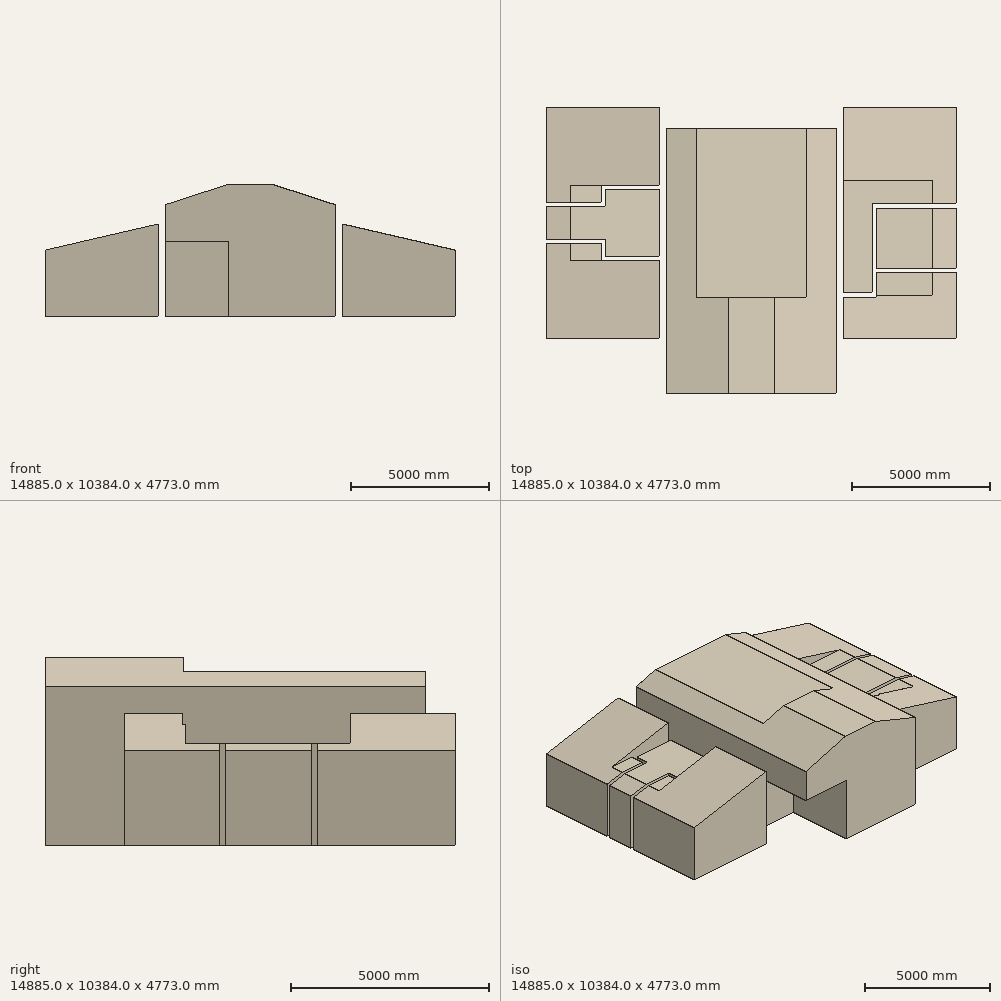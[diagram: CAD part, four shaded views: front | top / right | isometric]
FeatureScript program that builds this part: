
annotation { "Feature Type Name" : "Feature", "Feature Type Description" : "" }
export const myFeature = defineFeature(function(context is Context, id is Id, definition is map)
    precondition{}
    {
        {
            var Q0;
            Q0=qCreatedBy(makeId("Top.planeOp"),FACE);
            var sketch = newSketch(context, id + "F0", { "sketchPlane" : qUnion([Q0])});
            skLineSegment(sketch, "E0.bottom", {"start": v(1904.35, 18.05) * mm, "end": v(-95.65, 18.05) * mm});
            skLineSegment(sketch, "E0.top", {"start": v(3994.35, 3460.05) * mm, "end": v(-95.65, 3460.05) * mm});
            skLineSegment(sketch, "E0.left", {"start": v(3994.35, 618.05) * mm, "end": v(3994.35, 3460.05) * mm});
            skLineSegment(sketch, "E0.right", {"start": v(-95.65, 18.05) * mm, "end": v(-95.65, 3460.05) * mm});
            skLineSegment(sketch, "E1.top", {"start": v(3994.35, 618.05) * mm, "end": v(1904.35, 618.05) * mm});
            skLineSegment(sketch, "E1.right", {"start": v(1904.35, 18.05) * mm, "end": v(1904.35, 618.05) * mm});
            skSolve(sketch);
        }
        {
            var Q0;
            Q0 = qSketchRegion(id + "F0", true);
            extrude(context, id + "F1", {"entities" : qUnion([Q0]), "depth" : 4000 * mm, "offsetDistance" : 25 * mm});
        }
        {
            var Q0;
            Q0=makeQuery(id+"F1.opExtrude","CAP_FACE",FACE,{"disambiguationData":[OSD([sQuery(id+"F0.wireOp",EDGE,"E0.bottom"),sQuery(id+"F0.wireOp",EDGE,"E0.top"),sQuery(id+"F0.wireOp",EDGE,"E0.left"),sQuery(id+"F0.wireOp",EDGE,"E0.right"),sQuery(id+"F0.wireOp",EDGE,"E1.top"),sQuery(id+"F0.wireOp",EDGE,"E1.right")])],"isStart":true});
            var sketch = newSketch(context, id + "F2", { "sketchPlane" : qUnion([Q0])});
            skLineSegment(sketch, "E2", {"start": v(-95.65, 131.95) * mm, "end": v(2054.35, 131.95) * mm});
            skLineSegment(sketch, "E3", {"start": v(2054.35, 131.95) * mm, "end": v(2054.35, -468.05) * mm});
            skLineSegment(sketch, "E4", {"start": v(2054.35, -468.05) * mm, "end": v(3994.35, -468.05) * mm});
            skLineSegment(sketch, "E5", {"start": v(3994.35, -468.05) * mm, "end": v(3994.35, 1931.95) * mm});
            skLineSegment(sketch, "E6", {"start": v(3994.35, 1931.95) * mm, "end": v(2054.35, 1931.95) * mm});
            skLineSegment(sketch, "E7", {"start": v(2054.35, 1931.95) * mm, "end": v(2054.35, 1331.95) * mm});
            skLineSegment(sketch, "E8", {"start": v(2054.35, 1331.95) * mm, "end": v(-95.65, 1331.95) * mm});
            skLineSegment(sketch, "E9", {"start": v(-95.65, 1331.95) * mm, "end": v(-95.65, 131.95) * mm});
            skSolve(sketch);
        }
        {
            var Q0;
            Q0 = qSketchRegion(id + "F2", true);
            extrude(context, id + "F3", {"entities" : qUnion([Q0]), "oppositeDirection" : true, "depth" : 4000 * mm, "offsetDistance" : 25 * mm});
        }
        {
            var Q0;
            Q0=makeQuery(id+"F3.opExtrude","CAP_FACE",FACE,{"disambiguationData":[OSD([sQuery(id+"F2.wireOp",EDGE,"E2"),sQuery(id+"F2.wireOp",EDGE,"E3"),sQuery(id+"F2.wireOp",EDGE,"E4"),sQuery(id+"F2.wireOp",EDGE,"E5"),sQuery(id+"F2.wireOp",EDGE,"E6"),sQuery(id+"F2.wireOp",EDGE,"E7"),sQuery(id+"F2.wireOp",EDGE,"E8"),sQuery(id+"F2.wireOp",EDGE,"E9")])],"isStart":true});
            var sketch = newSketch(context, id + "F4", { "sketchPlane" : qUnion([Q0])});
            skLineSegment(sketch, "E10", {"start": v(-95.65, 1481.95) * mm, "end": v(1904.35, 1481.95) * mm});
            skLineSegment(sketch, "E11", {"start": v(1904.35, 1481.95) * mm, "end": v(1904.35, 2081.95) * mm});
            skLineSegment(sketch, "E12", {"start": v(1904.35, 2081.95) * mm, "end": v(3994.35, 2081.95) * mm});
            skLineSegment(sketch, "E13", {"start": v(3994.35, 2081.95) * mm, "end": v(3994.35, 4923.95) * mm});
            skLineSegment(sketch, "E14", {"start": v(3994.35, 4923.95) * mm, "end": v(-95.65, 4923.95) * mm});
            skLineSegment(sketch, "E15", {"start": v(-95.65, 4923.95) * mm, "end": v(-95.65, 1481.95) * mm});
            skSolve(sketch);
        }
        {
            var Q0;
            Q0 = qSketchRegion(id + "F4", true);
            extrude(context, id + "F5", {"entities" : qUnion([Q0]), "oppositeDirection" : true, "depth" : 4000 * mm, "offsetDistance" : 25 * mm});
        }
        {
            var Q0;
            Q0=makeQuery(id+"F5.opExtrude","SWEPT_FACE",FACE,{"disambiguationData":[OSD([sQuery(id+"F4.wireOp",EDGE,"E14")])]});
            var sketch = newSketch(context, id + "F6", { "sketchPlane" : qUnion([Q0])});
            skLineSegment(sketch, "E16", {"start": v(-95.65, 2400) * mm, "end": v(3994.35, 3344.25) * mm});
            skLineSegment(sketch, "E17", {"start": v(3994.35, 3344.25) * mm, "end": v(3994.35, 5219.77) * mm});
            skLineSegment(sketch, "E18", {"start": v(3994.35, 5219.77) * mm, "end": v(-95.65, 4000) * mm});
            skLineSegment(sketch, "E19", {"start": v(-95.65, 4000) * mm, "end": v(-95.65, 2400) * mm});
            skLineSegment(sketch, "E20", {"start": v(-95.65, 0) * mm, "end": v(3994.35, 0) * mm});
            skSolve(sketch);
        }
        {
            var Q0;
            Q0 = qSketchRegion(id + "F6", true);
            extrude(context, id + "F7", {"entities" : qUnion([Q0]), "operationType" : NewBodyOperationType.REMOVE, "oppositeDirection" : true, "depth" : 10000 * mm, "offsetDistance" : 25 * mm});
        }
        {
            var Q0;
            Q0=makeQuery(id+"F5.opExtrude","CAP_FACE",FACE,{"disambiguationData":[OSD([sQuery(id+"F4.wireOp",EDGE,"E10"),sQuery(id+"F4.wireOp",EDGE,"E11"),sQuery(id+"F4.wireOp",EDGE,"E12"),sQuery(id+"F4.wireOp",EDGE,"E13"),sQuery(id+"F4.wireOp",EDGE,"E14"),sQuery(id+"F4.wireOp",EDGE,"E15")])],"isStart":true});
            var sketch = newSketch(context, id + "F8", { "sketchPlane" : qUnion([Q0])});
            skLineSegment(sketch, "E21.bottom", {"start": v(4252.35, 6923.95) * mm, "end": v(10441.35, 6923.95) * mm});
            skLineSegment(sketch, "E21.top", {"start": v(4252.35, -2710.05) * mm, "end": v(10441.35, -2710.05) * mm});
            skLineSegment(sketch, "E21.left", {"start": v(4252.35, 6923.95) * mm, "end": v(4252.35, -2710.05) * mm});
            skLineSegment(sketch, "E21.right", {"start": v(10441.35, 6923.95) * mm, "end": v(10441.35, -2710.05) * mm});
            skSolve(sketch);
        }
        {
            var Q0;
            Q0 = qSketchRegion(id + "F8", true);
            extrude(context, id + "F9", {"entities" : qUnion([Q0]), "oppositeDirection" : true, "depth" : 6000 * mm, "offsetDistance" : 25 * mm});
        }
        {
            var Q0;
            Q0=makeQuery(id+"F9.opExtrude","SWEPT_FACE",FACE,{"disambiguationData":[OSD([sQuery(id+"F8.wireOp",EDGE,"E21.bottom")])]});
            var sketch = newSketch(context, id + "F10", { "sketchPlane" : qUnion([Q0])});
            skLineSegment(sketch, "E22", {"start": v(4252.35, 4042.28) * mm, "end": v(6501.16, 4772.96) * mm});
            skLineSegment(sketch, "E23", {"start": v(4252.35, 4042.28) * mm, "end": v(4252.35, 6000) * mm});
            skLineSegment(sketch, "E24", {"start": v(4252.35, 6000) * mm, "end": v(10441.35, 6000) * mm});
            skLineSegment(sketch, "E25", {"start": v(10441.35, 6000) * mm, "end": v(10441.35, 4042.28) * mm});
            skLineSegment(sketch, "E26", {"start": v(6501.16, 4772.96) * mm, "end": v(8192.54, 4772.96) * mm});
            skPoint(sketch, "E27.orphan", {"position": v(7346.85, 4200) * mm});
            skPoint(sketch, "E28.orphan", {"position": v(10441.35, 4200) * mm});
            skPoint(sketch, "E29.orphan", {"position": v(9926.23, 4772.96) * mm});
            skPoint(sketch, "E30.orphan", {"position": v(9926.23, 5005.46) * mm});
            skLineSegment(sketch, "E31.trimOffspring", {"start": v(8192.54, 4772.96) * mm, "end": v(10441.35, 4042.28) * mm});
            skPoint(sketch, "E32.orphan", {"position": v(7346.85, 5047.74) * mm});
            skPoint(sketch, "E33.orphan", {"position": v(7346.85, 5205.46) * mm});
            skPoint(sketch, "E34.start.orphan", {"position": v(5063.17, 5005.46) * mm});
            skPoint(sketch, "E35.orphan", {"position": v(5063.17, 4772.96) * mm});
            skSolve(sketch);
        }
        {
            var Q0;
            Q0=makeQuery(id+"F10.imprint","IMPRINT",FACE,{"disambiguationData":[TD([[makeQuery(id+"F10.imprint","IMPRINT",EDGE,{"derivedFrom":sQuery(id+"F10.wireOp",EDGE,"E22")}),1.0]])]});
            extrude(context, id + "F11", {"entities" : qUnion([Q0]), "operationType" : NewBodyOperationType.REMOVE, "oppositeDirection" : true, "depth" : 3500 * mm, "offsetDistance" : 25 * mm});
        }
        {
            var Q0;
            Q0=makeQuery(id+"F11.boolean.opBoolean","COPY",FACE,{"derivedFrom":makeQuery(id+"F11.opExtrude","CAP_FACE",FACE,{"disambiguationData":[OSD([sQuery(id+"F10.wireOp",EDGE,"E22"),sQuery(id+"F10.wireOp",EDGE,"E23"),sQuery(id+"F10.wireOp",EDGE,"E24"),sQuery(id+"F10.wireOp",EDGE,"E25"),sQuery(id+"F10.wireOp",EDGE,"E26"),sQuery(id+"F10.wireOp",EDGE,"E31.trimOffspring")])],"isStart":false})});
            var sketch = newSketch(context, id + "F12", { "sketchPlane" : qUnion([Q0])});
            skLineSegment(sketch, "E36.bottom", {"start": v(4252.35, 6000) * mm, "end": v(10421.32, 6000) * mm});
            skLineSegment(sketch, "E36.left", {"start": v(4252.35, 6000) * mm, "end": v(4252.35, 4042.28) * mm});
            skLineSegment(sketch, "E37", {"start": v(5353.3, 4400) * mm, "end": v(9340.4, 4400) * mm});
            skLineSegment(sketch, "E38", {"start": v(4252.35, 4042.28) * mm, "end": v(5353.3, 4400) * mm});
            skLineSegment(sketch, "E39", {"start": v(10441.35, 4042.28) * mm, "end": v(9340.4, 4400) * mm});
            skPoint(sketch, "E36.top.end.orphan", {"position": v(10421.32, 0) * mm});
            skLineSegment(sketch, "E40", {"start": v(10421.32, 4048.79) * mm, "end": v(10441.35, 4042.28) * mm});
            skLineSegment(sketch, "E41", {"start": v(10441.35, 4042.28) * mm, "end": v(10441.35, 6000) * mm});
            skLineSegment(sketch, "E42", {"start": v(10441.35, 6000) * mm, "end": v(10421.32, 6000) * mm});
            skSolve(sketch);
        }
        {
            var Q0;
            Q0 = qSketchRegion(id + "F12", true);
            extrude(context, id + "F13", {"entities" : qUnion([Q0]), "operationType" : NewBodyOperationType.REMOVE, "endBound" : BoundingType.THROUGH_ALL, "oppositeDirection" : true, "depth" : 25 * mm, "offsetDistance" : 25 * mm});
        }
        {
            var Q0;
            Q0=makeQuery(id+"F9.opExtrude","CAP_FACE",FACE,{"disambiguationData":[OSD([sQuery(id+"F8.wireOp",EDGE,"E21.bottom"),sQuery(id+"F8.wireOp",EDGE,"E21.top"),sQuery(id+"F8.wireOp",EDGE,"E21.left"),sQuery(id+"F8.wireOp",EDGE,"E21.right")])],"isStart":true});
            var sketch = newSketch(context, id + "F14", { "sketchPlane" : qUnion([Q0])});
            skLineSegment(sketch, "E43.bottom", {"start": v(4252.35, 6923.95) * mm, "end": v(6539.85, 6923.95) * mm});
            skLineSegment(sketch, "E43.top", {"start": v(4252.35, 3923.95) * mm, "end": v(6539.85, 3923.95) * mm});
            skLineSegment(sketch, "E43.left", {"start": v(4252.35, 6923.95) * mm, "end": v(4252.35, 3923.95) * mm});
            skLineSegment(sketch, "E43.right", {"start": v(6539.85, 6923.95) * mm, "end": v(6539.85, 3923.95) * mm});
            skSolve(sketch);
        }
        {
            var Q0;
            Q0 = qSketchRegion(id + "F14", true);
            extrude(context, id + "F15", {"entities" : qUnion([Q0]), "operationType" : NewBodyOperationType.REMOVE, "oppositeDirection" : true, "depth" : 2700 * mm, "offsetDistance" : 25 * mm});
        }
        {
            var Q0;
            Q0=makeQuery(id+"F1.opExtrude","CAP_FACE",FACE,{"disambiguationData":[OSD([sQuery(id+"F0.wireOp",EDGE,"E0.bottom"),sQuery(id+"F0.wireOp",EDGE,"E0.top"),sQuery(id+"F0.wireOp",EDGE,"E0.left"),sQuery(id+"F0.wireOp",EDGE,"E0.right"),sQuery(id+"F0.wireOp",EDGE,"E1.top"),sQuery(id+"F0.wireOp",EDGE,"E1.right")])],"isStart":true});
            var sketch = newSketch(context, id + "F16", { "sketchPlane" : qUnion([Q0])});
            skLineSegment(sketch, "E44.bottom", {"start": v(10699.35, -3460.05) * mm, "end": v(14789.35, -3460.05) * mm});
            skLineSegment(sketch, "E44.top", {"start": v(10699.35, 39.95) * mm, "end": v(14789.35, 39.95) * mm});
            skLineSegment(sketch, "E44.left", {"start": v(10699.35, -3460.05) * mm, "end": v(10699.35, 39.95) * mm});
            skLineSegment(sketch, "E44.right", {"start": v(14789.35, -3460.05) * mm, "end": v(14789.35, 39.95) * mm});
            skSolve(sketch);
        }
        {
            var Q0;
            Q0 = qSketchRegion(id + "F16", true);
            extrude(context, id + "F17", {"entities" : qUnion([Q0]), "oppositeDirection" : true, "depth" : 4000 * mm, "offsetDistance" : 25 * mm});
        }
        {
            var Q0;
            Q0=makeQuery(id+"F5.opExtrude","CAP_FACE",FACE,{"disambiguationData":[OSD([sQuery(id+"F4.wireOp",EDGE,"E10"),sQuery(id+"F4.wireOp",EDGE,"E11"),sQuery(id+"F4.wireOp",EDGE,"E12"),sQuery(id+"F4.wireOp",EDGE,"E13"),sQuery(id+"F4.wireOp",EDGE,"E14"),sQuery(id+"F4.wireOp",EDGE,"E15")])],"isStart":true});
            var sketch = newSketch(context, id + "F18", { "sketchPlane" : qUnion([Q0])});
            skLineSegment(sketch, "E45.bottom", {"start": v(10699.35, 4923.95) * mm, "end": v(14789.35, 4923.95) * mm});
            skLineSegment(sketch, "E45.top", {"start": v(10699.35, 3446) * mm, "end": v(11889.35, 3446) * mm});
            skLineSegment(sketch, "E45.left", {"start": v(10699.35, 4923.95) * mm, "end": v(10699.35, 3446) * mm});
            skLineSegment(sketch, "E45.right", {"start": v(14789.35, 4923.95) * mm, "end": v(14789.35, 3446) * mm});
            skLineSegment(sketch, "E46.top", {"start": v(14789.35, 2523.95) * mm, "end": v(11889.35, 2523.95) * mm});
            skLineSegment(sketch, "E46.left", {"start": v(14789.35, 3446) * mm, "end": v(14789.35, 2523.95) * mm});
            skLineSegment(sketch, "E46.right", {"start": v(11889.35, 3446) * mm, "end": v(11889.35, 2523.95) * mm});
            skSolve(sketch);
        }
        {
            var Q0;
            Q0=makeQuery(id+"F3.opExtrude","SWEPT_FACE",FACE,{"disambiguationData":[OSD([sQuery(id+"F2.wireOp",EDGE,"E9")])]});
            var sketch = newSketch(context, id + "F19", { "sketchPlane" : qUnion([Q0])});
            skLineSegment(sketch, "E47.top", {"start": v(2081.95, 2600) * mm, "end": v(-618.05, 2600) * mm});
            skLineSegment(sketch, "E48.top", {"start": v(2081.95, 4131.32) * mm, "end": v(-618.05, 4131.32) * mm});
            skLineSegment(sketch, "E48.left", {"start": v(2081.95, 2600) * mm, "end": v(2081.95, 4131.32) * mm});
            skLineSegment(sketch, "E48.right", {"start": v(-618.05, 2600) * mm, "end": v(-618.05, 4131.32) * mm});
            skPoint(sketch, "E47.left.start.orphan", {"position": v(2006.95, 0) * mm});
            skSolve(sketch);
        }
        {
            var Q0;
            Q0 = qSketchRegion(id + "F19", true);
            extrude(context, id + "F20", {"entities" : qUnion([Q0]), "operationType" : NewBodyOperationType.REMOVE, "oppositeDirection" : true, "depth" : 4090 * mm, "offsetDistance" : 25 * mm});
        }
        {
            var Q0;
            Q0 = qSketchRegion(id + "F18", true);
            extrude(context, id + "F21", {"entities" : qUnion([Q0]), "oppositeDirection" : true, "depth" : 4000 * mm, "offsetDistance" : 25 * mm});
        }
        {
            var Q0;
            Q0=makeQuery(id+"F17.opExtrude","CAP_FACE",FACE,{"disambiguationData":[OSD([sQuery(id+"F16.wireOp",EDGE,"E44.bottom"),sQuery(id+"F16.wireOp",EDGE,"E44.top"),sQuery(id+"F16.wireOp",EDGE,"E44.left"),sQuery(id+"F16.wireOp",EDGE,"E44.right")])],"isStart":true});
            var sketch = newSketch(context, id + "F22", { "sketchPlane" : qUnion([Q0])});
            skLineSegment(sketch, "E49", {"start": v(14789.35, 189.95) * mm, "end": v(11889.35, 189.95) * mm});
            skLineSegment(sketch, "E50", {"start": v(11889.35, 2373.95) * mm, "end": v(14789.35, 2373.95) * mm});
            skLineSegment(sketch, "E51", {"start": v(11889.35, 2373.95) * mm, "end": v(11889.35, 189.95) * mm});
            skLineSegment(sketch, "E52", {"start": v(14789.35, 189.95) * mm, "end": v(14789.35, 2373.95) * mm});
            skPoint(sketch, "E53.start.orphan", {"position": v(10699.35, 189.95) * mm});
            skSolve(sketch);
        }
        {
            var Q0;
            Q0 = qSketchRegion(id + "F22", true);
            extrude(context, id + "F23", {"entities" : qUnion([Q0]), "oppositeDirection" : true, "depth" : 4000 * mm, "offsetDistance" : 25 * mm});
        }
        {
            var Q0;
            Q0=makeQuery(id+"F21.opExtrude","SWEPT_FACE",FACE,{"disambiguationData":[OSD([sQuery(id+"F18.wireOp",EDGE,"E45.bottom")])]});
            var sketch = newSketch(context, id + "F24", { "sketchPlane" : qUnion([Q0])});
            skLineSegment(sketch, "E54.top", {"start": v(14789.35, 4000) * mm, "end": v(10699.35, 4000) * mm});
            skLineSegment(sketch, "E54.left", {"start": v(14789.35, 2400) * mm, "end": v(14789.35, 4000) * mm});
            skLineSegment(sketch, "E54.right", {"start": v(10699.35, 3344.25) * mm, "end": v(10699.35, 4000) * mm});
            skLineSegment(sketch, "E55", {"start": v(14789.35, 2400) * mm, "end": v(10699.35, 3344.25) * mm});
            skPoint(sketch, "E56.orphan", {"position": v(14789.35, 0) * mm});
            skSolve(sketch);
        }
        {
            var Q0;
            Q0=makeQuery(id+"F24.imprint","IMPRINT",FACE,{"disambiguationData":[TD([[makeQuery(id+"F24.imprint","IMPRINT",EDGE,{"derivedFrom":sQuery(id+"F24.wireOp",EDGE,"E54.top")}),-1.0]])]});
            extrude(context, id + "F25", {"entities" : qUnion([Q0]), "operationType" : NewBodyOperationType.REMOVE, "endBound" : BoundingType.THROUGH_ALL, "oppositeDirection" : true, "depth" : 25 * mm, "offsetDistance" : 25 * mm});
        }
        {
            var Q0;
            Q0=makeQuery(id+"F23.opExtrude","SWEPT_FACE",FACE,{"disambiguationData":[OSD([sQuery(id+"F22.wireOp",EDGE,"E52")])]});
            var sketch = newSketch(context, id + "F26", { "sketchPlane" : qUnion([Q0])});
            skLineSegment(sketch, "E57.top", {"start": v(810.05, 3600) * mm, "end": v(-3373.95, 3600) * mm});
            skLineSegment(sketch, "E57.left", {"start": v(810.05, 2600) * mm, "end": v(810.05, 3600) * mm});
            skLineSegment(sketch, "E57.right", {"start": v(-3373.95, 2600) * mm, "end": v(-3373.95, 3600) * mm});
            skLineSegment(sketch, "E58", {"start": v(-3373.95, 2600) * mm, "end": v(810.05, 2600) * mm});
            skPoint(sketch, "E59.orphan", {"position": v(810.05, 0) * mm});
            skSolve(sketch);
        }
        {
            var Q0;
            Q0=makeQuery(id+"F26.imprint","IMPRINT",FACE,{"disambiguationData":[TD([[makeQuery(id+"F26.imprint","IMPRINT",EDGE,{"derivedFrom":sQuery(id+"F26.wireOp",EDGE,"E57.top")}),1.0]])]});
            extrude(context, id + "F27", {"entities" : qUnion([Q0]), "operationType" : NewBodyOperationType.REMOVE, "oppositeDirection" : true, "depth" : 4090 * mm, "offsetDistance" : 25 * mm});
        }
        {
            var Q0;
            Q0=makeQuery(id+"F17.opExtrude","SWEPT_FACE",FACE,{"disambiguationData":[OSD([sQuery(id+"F16.wireOp",EDGE,"E44.top")])]});
            var sketch = newSketch(context, id + "F28", { "sketchPlane" : qUnion([Q0])});
            skLineSegment(sketch, "E60.bottom", {"start": v(10699.35, 0) * mm, "end": v(11739.35, 0) * mm});
            skLineSegment(sketch, "E60.top", {"start": v(10699.35, 2600) * mm, "end": v(11739.35, 2600) * mm});
            skLineSegment(sketch, "E60.left", {"start": v(10699.35, 0) * mm, "end": v(10699.35, 2600) * mm});
            skLineSegment(sketch, "E60.right", {"start": v(11739.35, 0) * mm, "end": v(11739.35, 2600) * mm});
            skSolve(sketch);
        }
        {
            var Q0;
            Q0=makeQuery(id+"F28.imprint","IMPRINT",FACE,{"disambiguationData":[TD([[makeQuery(id+"F28.imprint","IMPRINT",EDGE,{"derivedFrom":sQuery(id+"F28.wireOp",EDGE,"E60.bottom")}),1.0]])]});
            extrude(context, id + "F29", {"entities" : qUnion([Q0]), "operationType" : NewBodyOperationType.ADD, "depth" : 3200 * mm, "offsetDistance" : 25 * mm});
        }
    });
